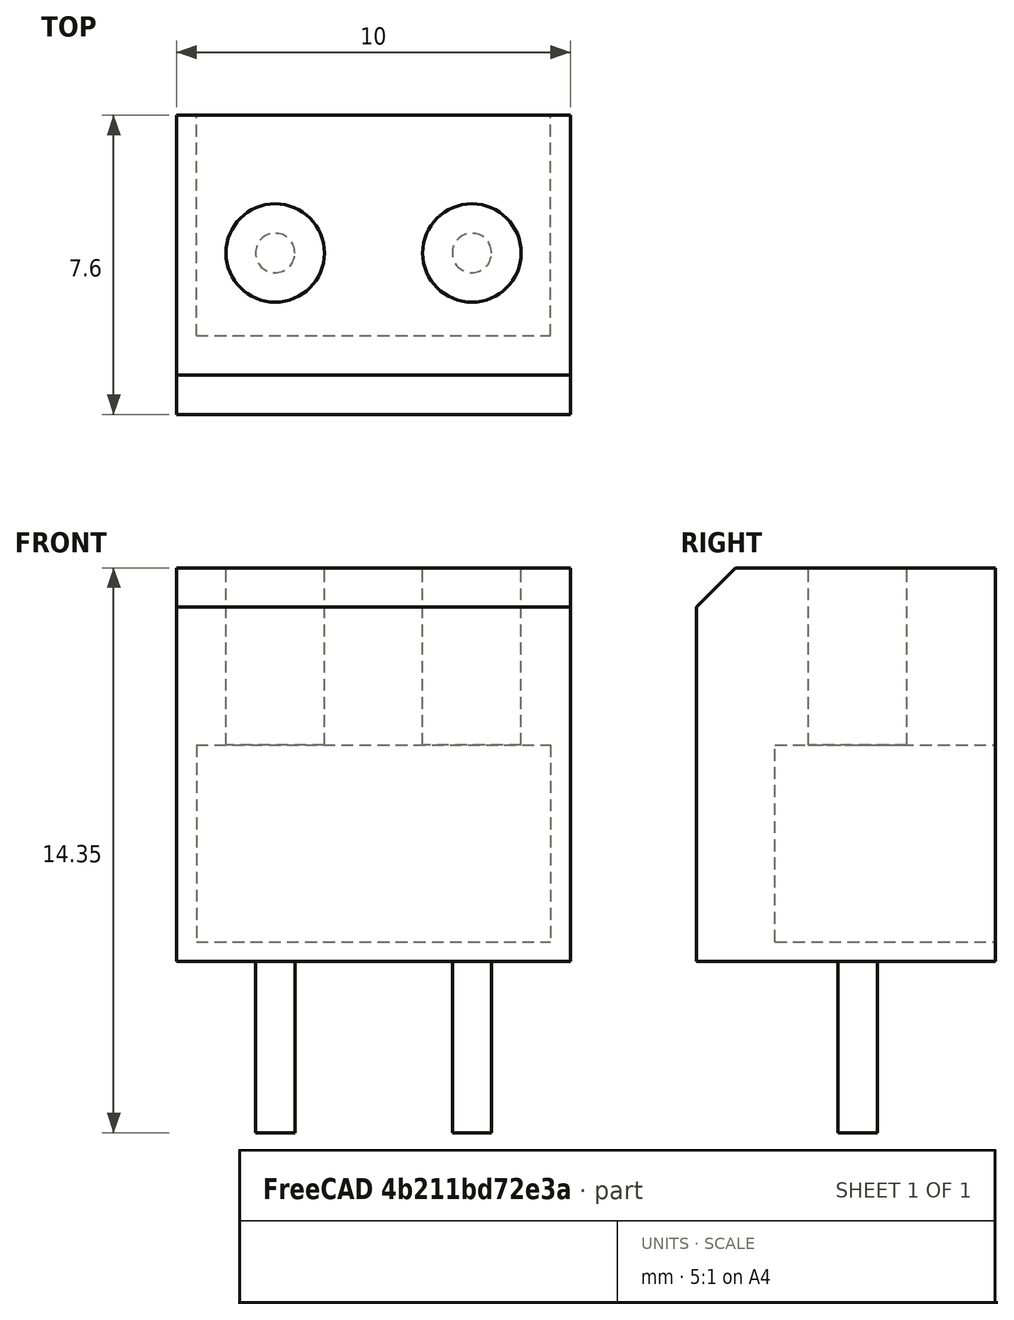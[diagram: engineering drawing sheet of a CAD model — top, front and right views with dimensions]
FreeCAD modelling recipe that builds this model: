
FCSTD DOCUMENT  (FreeCAD 0.18R4 (GitTag))
Label: terminalblock
License: All rights reserved
LicenseURL: http://en.wikipedia.org/wiki/All_rights_reserved
objects: Part::Cylinder×4, Part::Cut×3, Part::Box×2, App::Part×1, Part::Chamfer×1
note: 10 computed .brp shape members not serialized (recipe doc carries the construction recipe); baked Part::Feature solids carry a one-line shape summary decoded from their .brp

FEATURE [App::Part] Part
  Origin = -> Origin
FEATURE [Part::Box] Box  label="Cube"
  AttacherType = Attacher::AttachEngine3D
  Height = 10
  Length = 10
  Width = 7.6
FEATURE [Part::Cylinder] Cylinder
  Angle = 360
  AttacherType = Attacher::AttachEngine3D
  Height = 4.35
  Placement = pos=(2.5,4.1,-4.35) rot=(0,0,1;0rad)
  Radius = 0.5
FEATURE [Part::Cylinder] Cylinder001
  Angle = 360
  AttacherType = Attacher::AttachEngine3D
  Height = 4.35
  Placement = pos=(7.5,4.1,-4.35) rot=(0,0,1;0rad)
  Radius = 0.5
FEATURE [Part::Cylinder] Cylinder002
  Angle = 360
  AttacherType = Attacher::AttachEngine3D
  Height = 5
  Placement = pos=(2.5,4.1,5) rot=(0,0,1;0rad)
  Radius = 1.25
FEATURE [Part::Cut] Cut
  Base = -> Box
  Tool = -> Cylinder002
FEATURE [Part::Cylinder] Cylinder003
  Angle = 360
  AttacherType = Attacher::AttachEngine3D
  Height = 5
  Placement = pos=(7.5,4.1,5) rot=(0,0,1;0rad)
  Radius = 1.25
FEATURE [Part::Cut] Cut001
  Base = -> Cut
  Tool = -> Cylinder003
FEATURE [Part::Box] Box001  label="Cube001"
  AttacherType = Attacher::AttachEngine3D
  Height = 5
  Length = 9
  Placement = pos=(0.5,2,0.5) rot=(0,0,1;0rad)
  Width = 6
FEATURE [Part::Cut] Cut002
  Base = -> Cut001
  Tool = -> Box001
FEATURE [Part::Chamfer] Chamfer
  Base = -> Cut002
  Edges = 1 edges r=1: [Edge7]
